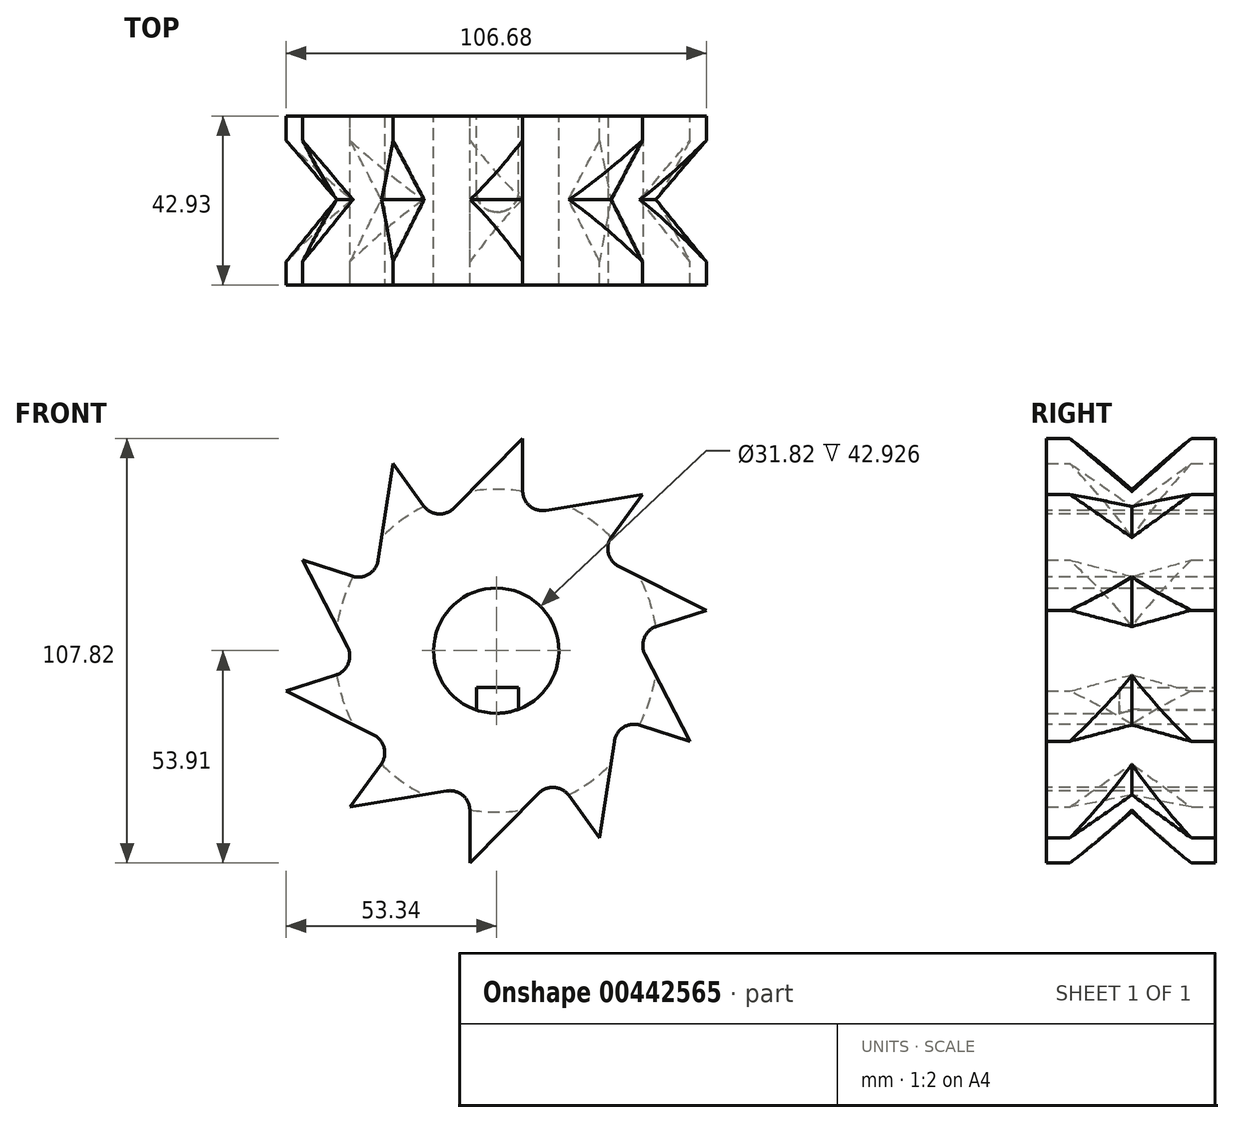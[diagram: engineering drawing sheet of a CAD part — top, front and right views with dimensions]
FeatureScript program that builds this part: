
annotation { "Feature Type Name" : "Feature", "Feature Type Description" : "" }
export const myFeature = defineFeature(function(context is Context, id is Id, definition is map)
    precondition{}
    {
        {
            var Q0;
            Q0=qCreatedBy(makeId("Front.planeOp"),FACE);
            var sketch = newSketch(context, id + "F0", { "sketchPlane" : qUnion([Q0])});
            skLineSegment(sketch, "E0", {"start": v(-14.95, 31.98) * mm, "end": v(6.7, 53.9) * mm});
            skLineSegment(sketch, "E1", {"start": v(6.7, 53.9) * mm, "end": v(6.7, 34.66) * mm});
            skLineSegment(sketch, "E2.1.0", {"start": v(-30.9, 17.09) * mm, "end": v(-26.26, 47.55) * mm});
            skLineSegment(sketch, "E2.1.1", {"start": v(-26.26, 47.55) * mm, "end": v(-14.95, 31.98) * mm});
            skLineSegment(sketch, "E2.2.0", {"start": v(-35.03, -4.33) * mm, "end": v(-49.2, 23.03) * mm});
            skLineSegment(sketch, "E2.2.1", {"start": v(-49.2, 23.03) * mm, "end": v(-30.9, 17.09) * mm});
            skLineSegment(sketch, "E2.3.0", {"start": v(-25.8, -24.1) * mm, "end": v(-53.34, -10.28) * mm});
            skLineSegment(sketch, "E2.3.1", {"start": v(-53.34, -10.28) * mm, "end": v(-35.03, -4.33) * mm});
            skLineSegment(sketch, "E2.4.0", {"start": v(-6.7, -34.66) * mm, "end": v(-37.1, -39.67) * mm});
            skLineSegment(sketch, "E2.4.1", {"start": v(-37.1, -39.67) * mm, "end": v(-25.8, -24.1) * mm});
            skLineSegment(sketch, "E2.5.0", {"start": v(14.95, -31.98) * mm, "end": v(-6.7, -53.9) * mm});
            skLineSegment(sketch, "E2.5.1", {"start": v(-6.7, -53.9) * mm, "end": v(-6.7, -34.66) * mm});
            skLineSegment(sketch, "E2.6.0", {"start": v(30.9, -17.09) * mm, "end": v(26.26, -47.55) * mm});
            skLineSegment(sketch, "E2.6.1", {"start": v(26.26, -47.55) * mm, "end": v(14.95, -31.98) * mm});
            skLineSegment(sketch, "E2.7.0", {"start": v(35.03, 4.33) * mm, "end": v(49.2, -23.03) * mm});
            skLineSegment(sketch, "E2.7.1", {"start": v(49.2, -23.03) * mm, "end": v(30.9, -17.09) * mm});
            skLineSegment(sketch, "E2.8.0", {"start": v(25.8, 24.1) * mm, "end": v(53.34, 10.28) * mm});
            skLineSegment(sketch, "E2.8.1", {"start": v(53.34, 10.28) * mm, "end": v(35.03, 4.33) * mm});
            skLineSegment(sketch, "E2.9.0", {"start": v(6.7, 34.66) * mm, "end": v(37.1, 39.67) * mm});
            skLineSegment(sketch, "E2.9.1", {"start": v(37.1, 39.67) * mm, "end": v(25.8, 24.1) * mm});
            skPoint(sketch, "E2.center", {"position": v(0, 0) * mm});
            skCircle(sketch, "E3", {"center": v(0, 0) * mm, "radius": 15.9 * mm});
            skLineSegment(sketch, "E4", {"start": v(5.63, -14.88) * mm, "end": v(5.63, -9.31) * mm});
            skLineSegment(sketch, "E5", {"start": v(5.63, -9.31) * mm, "end": v(-5.04, -9.31) * mm});
            skLineSegment(sketch, "E6", {"start": v(-5.04, -9.31) * mm, "end": v(-5.04, -15.1) * mm});
            skSolve(sketch);
        }
        {
            var Q0;
            Q0=makeQuery(id+"F0.imprint","IMPRINT",FACE,{"disambiguationData":[TD([[makeQuery(id+"F0.imprint","IMPRINT",EDGE,{"derivedFrom":sQuery(id+"F0.wireOp",EDGE,"E0")}),-1.0]])]});
            extrude(context, id + "F1", {"entities" : qUnion([Q0]), "depth" : 42.93 * mm});
        }
        {
            var Q0;
            Q0=makeQuery(id+"F1.opExtrude","SWEPT_EDGE",EDGE,{"disambiguationData":[OSD([sQuery(id+"F0.wireOp",EDGE,"E2.8.0"),sQuery(id+"F0.wireOp",EDGE,"E2.9.1")])]});
            var Q1;
            Q1=makeQuery(id+"F1.opExtrude","SWEPT_EDGE",EDGE,{"disambiguationData":[OSD([sQuery(id+"F0.wireOp",EDGE,"E1"),sQuery(id+"F0.wireOp",EDGE,"E2.9.0")])]});
            var Q2;
            Q2=makeQuery(id+"F1.opExtrude","SWEPT_EDGE",EDGE,{"disambiguationData":[OSD([sQuery(id+"F0.wireOp",EDGE,"E2.7.0"),sQuery(id+"F0.wireOp",EDGE,"E2.8.1")])]});
            var Q3;
            Q3=makeQuery(id+"F1.opExtrude","SWEPT_EDGE",EDGE,{"disambiguationData":[OSD([sQuery(id+"F0.wireOp",EDGE,"E2.6.0"),sQuery(id+"F0.wireOp",EDGE,"E2.7.1")])]});
            var Q4;
            Q4=makeQuery(id+"F1.opExtrude","SWEPT_EDGE",EDGE,{"disambiguationData":[OSD([sQuery(id+"F0.wireOp",EDGE,"E2.5.0"),sQuery(id+"F0.wireOp",EDGE,"E2.6.1")])]});
            var Q5;
            Q5=makeQuery(id+"F1.opExtrude","SWEPT_EDGE",EDGE,{"disambiguationData":[OSD([sQuery(id+"F0.wireOp",EDGE,"E2.4.0"),sQuery(id+"F0.wireOp",EDGE,"E2.5.1")])]});
            var Q6;
            Q6=makeQuery(id+"F1.opExtrude","SWEPT_EDGE",EDGE,{"disambiguationData":[OSD([sQuery(id+"F0.wireOp",EDGE,"E2.3.0"),sQuery(id+"F0.wireOp",EDGE,"E2.4.1")])]});
            var Q7;
            Q7=makeQuery(id+"F1.opExtrude","SWEPT_EDGE",EDGE,{"disambiguationData":[OSD([sQuery(id+"F0.wireOp",EDGE,"E2.2.0"),sQuery(id+"F0.wireOp",EDGE,"E2.3.1")])]});
            var Q8;
            Q8=makeQuery(id+"F1.opExtrude","SWEPT_EDGE",EDGE,{"disambiguationData":[OSD([sQuery(id+"F0.wireOp",EDGE,"E2.1.0"),sQuery(id+"F0.wireOp",EDGE,"E2.2.1")])]});
            var Q9;
            Q9=makeQuery(id+"F1.opExtrude","SWEPT_EDGE",EDGE,{"disambiguationData":[OSD([sQuery(id+"F0.wireOp",EDGE,"E0"),sQuery(id+"F0.wireOp",EDGE,"E2.1.1")])]});
            fillet(context, id + "F2", {"entities" : qUnion([Q0, Q1, Q2, Q3, Q4, Q5, Q6, Q7, Q8, Q9]), "radius" : 5.08 * mm, "tangentPropagation" : true, "allowEdgeOverflow" : false});
        }
        {
            var Q0;
            Q0=qCreatedBy(makeId("Right.planeOp"),FACE);
            var sketch = newSketch(context, id + "F3", { "sketchPlane" : qUnion([Q0])});
            skLineSegment(sketch, "E7", {"start": v(-37.08, 54.4) * mm, "end": v(-21.22, 40.98) * mm});
            skLineSegment(sketch, "E8", {"start": v(-21.22, 40.98) * mm, "end": v(-6.1, 54.4) * mm});
            skLineSegment(sketch, "E9", {"start": v(-6.1, 54.4) * mm, "end": v(-37.08, 54.4) * mm});
            skLineSegment(sketch, "E10", {"start": v(-57.32, 0) * mm, "end": v(0, 0) * mm});
            skSolve(sketch);
        }
        {
            var Q0;
            Q0=makeQuery(id+"F3.imprint","IMPRINT",FACE,{"disambiguationData":[TD([[makeQuery(id+"F3.imprint","IMPRINT",EDGE,{"derivedFrom":sQuery(id+"F3.wireOp",EDGE,"E7")}),1.0]])]});
            var Q1;
            Q1=sQuery(id+"F3.wireOp",EDGE,"E10");
            revolve(context, id + "F4", {"operationType" : NewBodyOperationType.REMOVE, "entities" : qUnion([Q0]), "axis" : qUnion([Q1]), "revolveType" : RevolveType.FULL, "oppositeDirection" : true});
        }
        {
            var Q0;
            {var subQ0=sQuery(id+"F0.wireOp",EDGE,"E4");Q0=makeQuery(id+"F0.imprint","IMPRINT",FACE,{"disambiguationData":[TD([[makeQuery(id+"F0.imprint","IMPRINT",EDGE,{"derivedFrom":subQ0}),1.0]])]});}
            extrude(context, id + "F5", {"entities" : qUnion([Q0]), "operationType" : NewBodyOperationType.ADD, "depth" : 24.38 * mm});
        }
        {
            var Q0;
            Q0=makeQuery(id+"F5.opExtrude","CAP_EDGE",EDGE,{"disambiguationData":[OSD([sQuery(id+"F0.wireOp",EDGE,"E4")])],"isStart":false});
            var Q1;
            Q1=makeQuery(id+"F5.opExtrude","CAP_EDGE",EDGE,{"disambiguationData":[OSD([sQuery(id+"F0.wireOp",EDGE,"E6")])],"isStart":false});
            fillet(context, id + "F6", {"entities" : qUnion([Q0, Q1]), "radius" : 5.08 * mm, "tangentPropagation" : true, "allowEdgeOverflow" : false});
        }
    });
